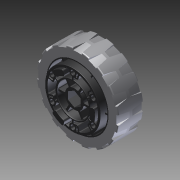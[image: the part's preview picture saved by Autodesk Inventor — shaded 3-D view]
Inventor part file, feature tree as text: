
AUTODESK INVENTOR PART (.ipt)
format: ipt  version: 2012 (Build 160160000, 160)  size: 3,137,536 bytes
history: native  units: in
note: dims shown in document units (in); Inventor stores cm internally (conversion verified against a paired STEP export)
features: fillet x2, imported_body x2, other x1
ambient origin geometry x8: Origin, YZ Plane, XZ Plane, XY Plane, X Axis, Y Axis, Z Axis, Center Point
feature tree (5):
  fillet  "Fillet6"  [1 undecoded]
  other  "217-3238-STEP1"
  fillet  "Fillet7"  [1 undecoded]
  imported_body  "Base1"
  imported_body  "Base2"
note: 2 required parameter values undecoded (feature->parameter linkage not recoverable at this tier; creation-order binding heuristic only, values carry confidence <= 0.55)
